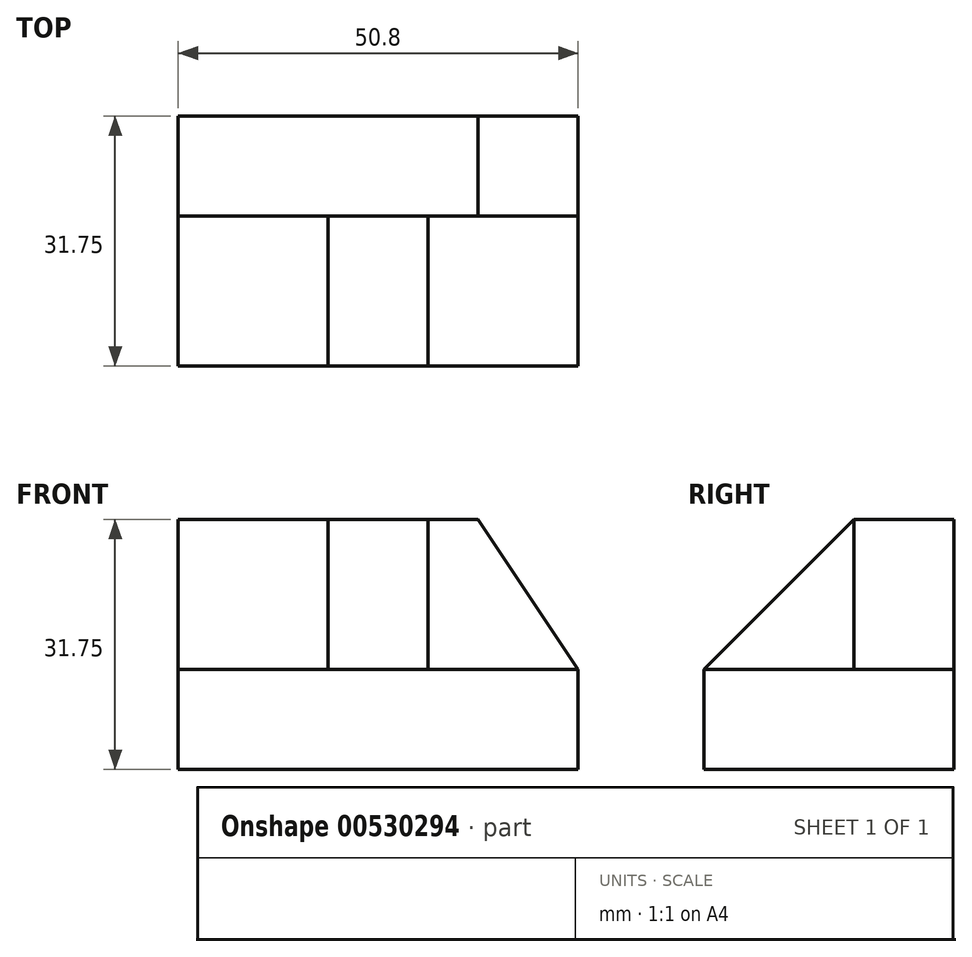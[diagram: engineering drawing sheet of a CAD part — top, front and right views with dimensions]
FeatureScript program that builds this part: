
annotation { "Feature Type Name" : "Feature", "Feature Type Description" : "" }
export const myFeature = defineFeature(function(context is Context, id is Id, definition is map)
    precondition{}
    {
        {
            var Q0;
            Q0=qCreatedBy(makeId("Front.planeOp"),FACE);
            var sketch = newSketch(context, id + "F0", { "sketchPlane" : qUnion([Q0])});
            skLineSegment(sketch, "E0", {"start": v(-31.83, 31.75) * mm, "end": v(-31.83, 0) * mm});
            skLineSegment(sketch, "E1", {"start": v(18.97, 0) * mm, "end": v(18.97, 31.75) * mm});
            skLineSegment(sketch, "E2", {"start": v(-31.83, 31.75) * mm, "end": v(18.97, 31.75) * mm});
            skLineSegment(sketch, "E3", {"start": v(-31.83, 0) * mm, "end": v(18.97, 0) * mm});
            skSolve(sketch);
        }
        {
            var Q0;
            Q0=makeQuery(id+"F0.imprint","IMPRINT",FACE,{"disambiguationData":[TD([[makeQuery(id+"F0.imprint","IMPRINT",EDGE,{"derivedFrom":sQuery(id+"F0.wireOp",EDGE,"E0")}),1.0]])]});
            extrude(context, id + "F1", {"entities" : qUnion([Q0]), "depth" : 31.75 * mm, "offsetDistance" : 25.4 * mm});
        }
        {
            var Q0;
            Q0=makeQuery(id+"F1.opExtrude","CAP_FACE",FACE,{"disambiguationData":[OSD([sQuery(id+"F0.wireOp",EDGE,"E0"),sQuery(id+"F0.wireOp",EDGE,"E1"),sQuery(id+"F0.wireOp",EDGE,"E2"),sQuery(id+"F0.wireOp",EDGE,"E3")])],"isStart":false});
            var sketch = newSketch(context, id + "F2", { "sketchPlane" : qUnion([Q0])});
            skLineSegment(sketch, "E4", {"start": v(-12.78, 31.75) * mm, "end": v(-12.78, 12.7) * mm});
            skLineSegment(sketch, "E5", {"start": v(-12.78, 12.7) * mm, "end": v(-31.83, 12.7) * mm});
            skSolve(sketch);
        }
        {
            var Q0;
            {var subQ0=sQuery(id+"F2.wireOp",EDGE,"E4");Q0=makeQuery(id+"F2.imprint","IMPRINT",FACE,{"disambiguationData":[TD([[makeQuery(id+"F2.imprint","IMPRINT",EDGE,{"derivedFrom":subQ0}),-1.0]])]});}
            extrude(context, id + "F3", {"entities" : qUnion([Q0]), "operationType" : NewBodyOperationType.REMOVE, "oppositeDirection" : true, "depth" : 19.05 * mm, "offsetDistance" : 25.4 * mm});
        }
        {
            var Q0;
            Q0=makeQuery(id+"F1.opExtrude","CAP_FACE",FACE,{"disambiguationData":[OSD([sQuery(id+"F0.wireOp",EDGE,"E0"),sQuery(id+"F0.wireOp",EDGE,"E1"),sQuery(id+"F0.wireOp",EDGE,"E2"),sQuery(id+"F0.wireOp",EDGE,"E3")])],"isStart":false});
            var sketch = newSketch(context, id + "F4", { "sketchPlane" : qUnion([Q0])});
            skLineSegment(sketch, "E6", {"start": v(-0.08, 31.75) * mm, "end": v(-0.08, 12.7) * mm});
            skLineSegment(sketch, "E7", {"start": v(-0.08, 12.7) * mm, "end": v(18.97, 12.7) * mm});
            skSolve(sketch);
        }
        {
            var Q0;
            {var subQ0=sQuery(id+"F4.wireOp",EDGE,"E6");Q0=makeQuery(id+"F4.imprint","IMPRINT",FACE,{"disambiguationData":[TD([[makeQuery(id+"F4.imprint","IMPRINT",EDGE,{"derivedFrom":subQ0}),1.0]])]});}
            extrude(context, id + "F5", {"entities" : qUnion([Q0]), "operationType" : NewBodyOperationType.REMOVE, "oppositeDirection" : true, "depth" : 19.05 * mm, "offsetDistance" : 25.4 * mm});
        }
        {
            var Q0;
            Q0=makeQuery(id+"F5.boolean.opBoolean","COPY",FACE,{"derivedFrom":makeQuery(id+"F5.opExtrude","CAP_FACE",FACE,{"disambiguationData":[OSD([sQuery(id+"F0.wireOp",EDGE,"E1"),sQuery(id+"F0.wireOp",EDGE,"E2"),sQuery(id+"F4.wireOp",EDGE,"E6"),sQuery(id+"F4.wireOp",EDGE,"E7")])],"isStart":false})});
            var sketch = newSketch(context, id + "F6", { "sketchPlane" : qUnion([Q0])});
            skLineSegment(sketch, "E8", {"start": v(6.27, 31.75) * mm, "end": v(18.97, 12.7) * mm});
            skSolve(sketch);
        }
        {
            var Q0;
            {var subQ0=sQuery(id+"F6.wireOp",EDGE,"E8");Q0=makeQuery(id+"F6.imprint","IMPRINT",FACE,{"disambiguationData":[TD([[makeQuery(id+"F6.imprint","IMPRINT",EDGE,{"derivedFrom":subQ0}),1.0]])]});}
            extrude(context, id + "F7", {"entities" : qUnion([Q0]), "operationType" : NewBodyOperationType.REMOVE, "oppositeDirection" : true, "depth" : 12.7 * mm, "offsetDistance" : 25.4 * mm});
        }
        {
            var Q0;
            Q0=makeQuery(id+"F5.boolean.opBoolean","COPY",FACE,{"derivedFrom":makeQuery(id+"F5.opExtrude","SWEPT_FACE",FACE,{"disambiguationData":[OSD([sQuery(id+"F4.wireOp",EDGE,"E6")])]})});
            var sketch = newSketch(context, id + "F8", { "sketchPlane" : qUnion([Q0])});
            skLineSegment(sketch, "E9", {"start": v(-12.7, 31.75) * mm, "end": v(-31.75, 12.7) * mm});
            skSolve(sketch);
        }
        {
            var Q0;
            Q0=makeQuery(id+"F8.imprint","IMPRINT",FACE,{"disambiguationData":[TD([[makeQuery(id+"F8.imprint","IMPRINT",EDGE,{"derivedFrom":sQuery(id+"F8.wireOp",EDGE,"E9")}),-1.0]])]});
            extrude(context, id + "F9", {"entities" : qUnion([Q0]), "operationType" : NewBodyOperationType.REMOVE, "oppositeDirection" : true, "depth" : 12.7 * mm, "offsetDistance" : 25.4 * mm});
        }
    });
